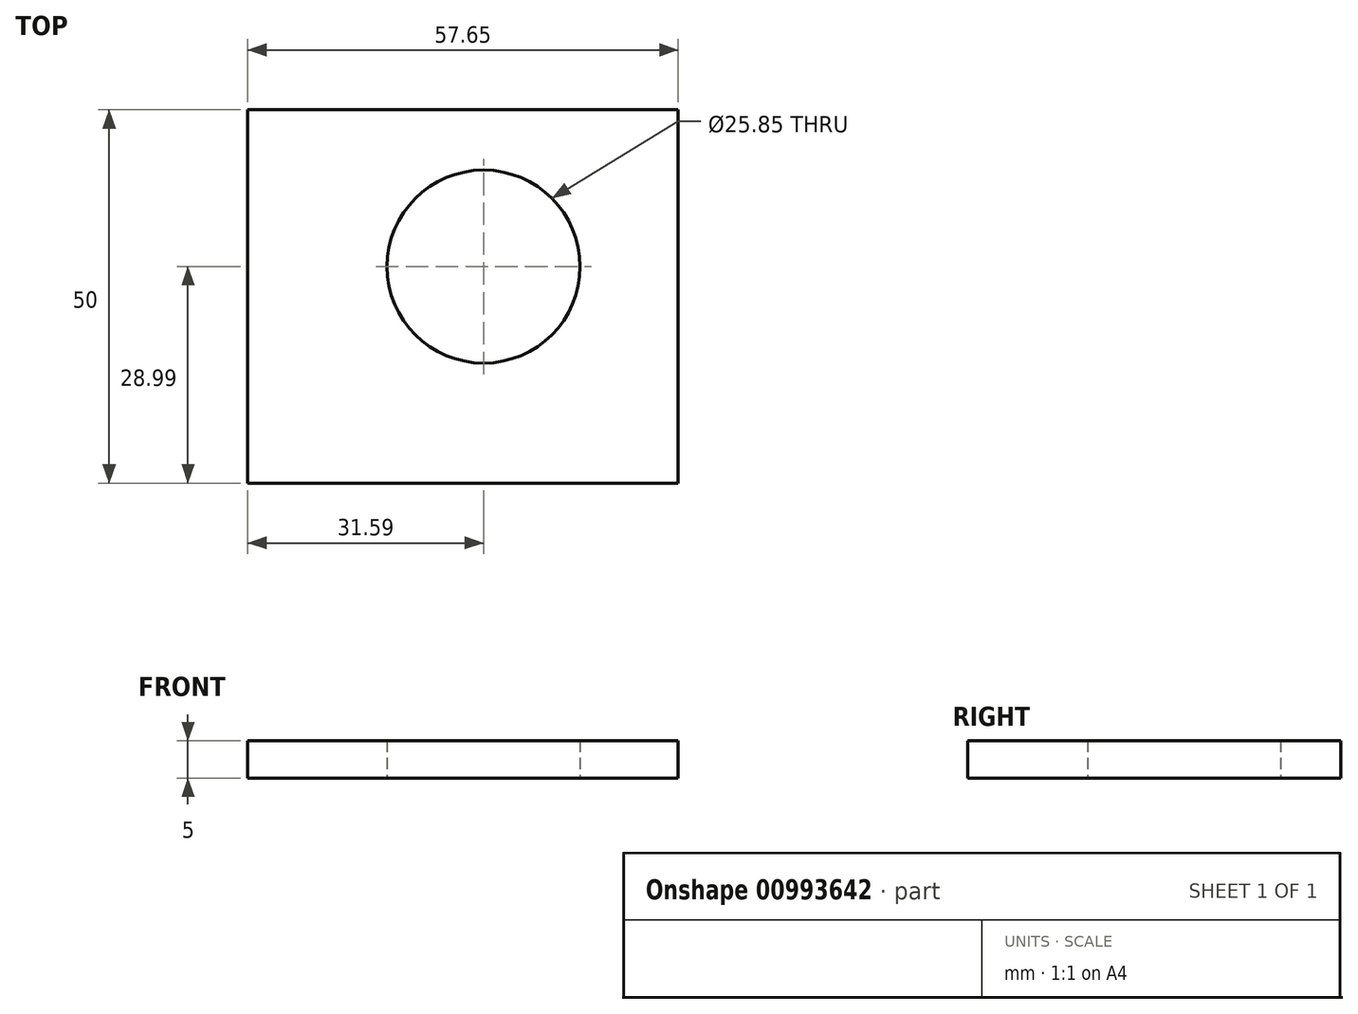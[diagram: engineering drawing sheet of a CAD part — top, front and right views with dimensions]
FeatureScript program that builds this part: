
annotation { "Feature Type Name" : "Feature", "Feature Type Description" : "" }
export const myFeature = defineFeature(function(context is Context, id is Id, definition is map)
    precondition{}
    {
        {
            var Q0;
            Q0=qCreatedBy(makeId("Top.planeOp"),FACE);
            var sketch = newSketch(context, id + "F0", { "sketchPlane" : qUnion([Q0])});
            skLineSegment(sketch, "E0.bottom", {"start": v(-31.59, 21) * mm, "end": v(26.06, 21) * mm});
            skLineSegment(sketch, "E0.top", {"start": v(-31.59, -29) * mm, "end": v(26.06, -29) * mm});
            skLineSegment(sketch, "E0.left", {"start": v(-31.59, 21) * mm, "end": v(-31.59, -29) * mm});
            skLineSegment(sketch, "E0.right", {"start": v(26.06, 21) * mm, "end": v(26.06, -29) * mm});
            skCircle(sketch, "E1", {"center": v(0, 0) * mm, "radius": 12.93 * mm});
            skSolve(sketch);
        }
        {
            var Q0;
            Q0=makeQuery(id+"F0.imprint","IMPRINT",FACE,{"disambiguationData":[TD([[makeQuery(id+"F0.imprint","IMPRINT",EDGE,{"derivedFrom":sQuery(id+"F0.wireOp",EDGE,"E0.bottom")}),-1.0]])]});
            extrude(context, id + "F1", {"entities" : qUnion([Q0]), "endBound" : BoundingType.SYMMETRIC, "depth" : 5 * mm, "offsetDistance" : 25 * mm});
        }
    });
